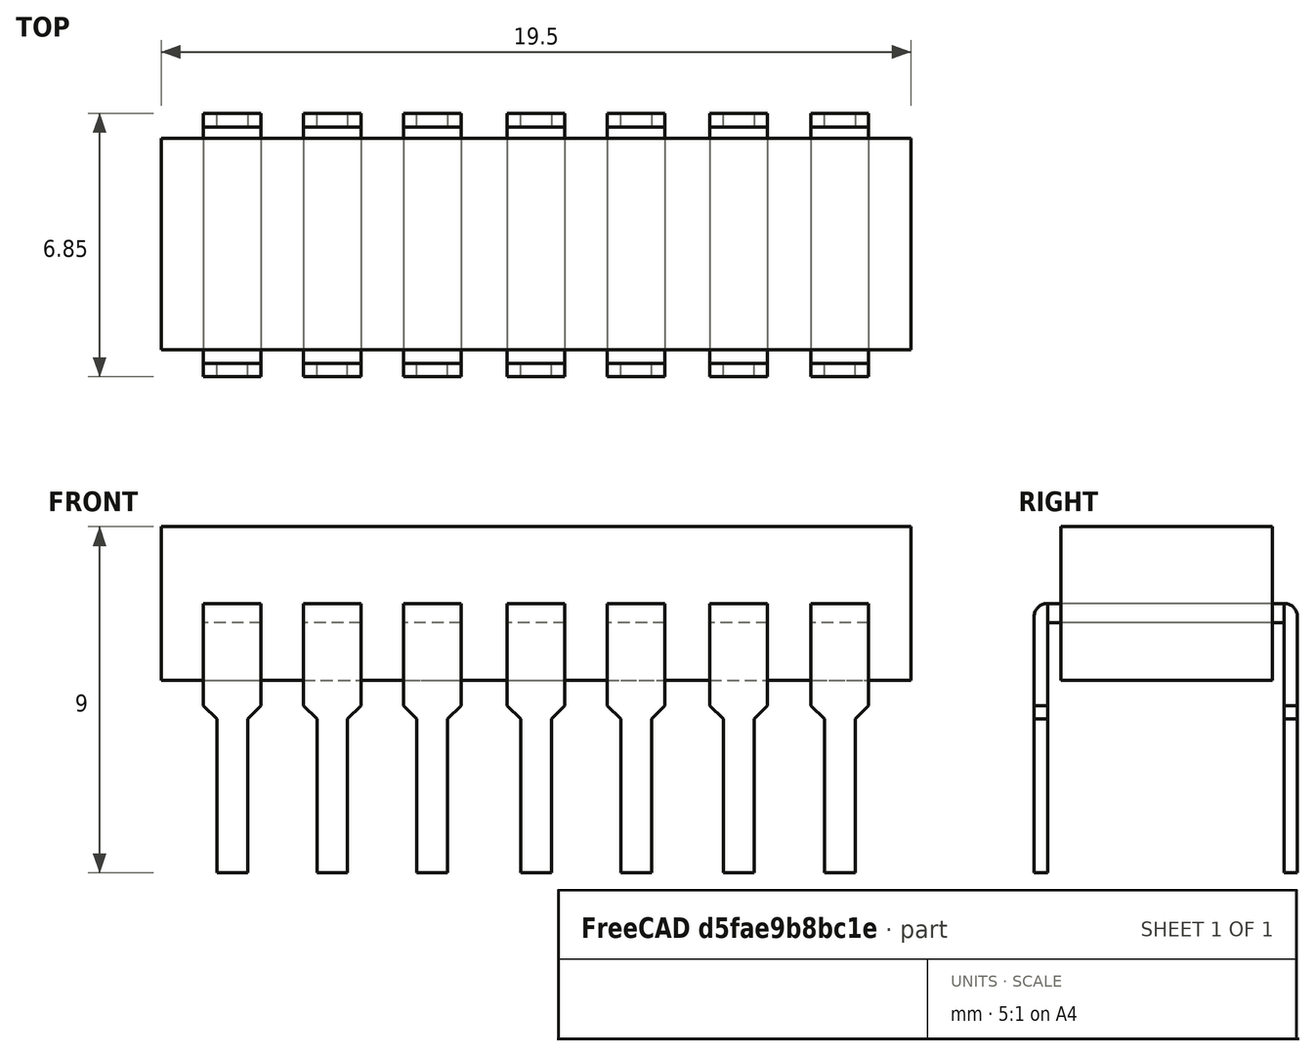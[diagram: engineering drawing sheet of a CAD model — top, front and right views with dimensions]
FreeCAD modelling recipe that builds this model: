
FCSTD DOCUMENT  (FreeCAD 1.0R39319 (Git))
Label: microshem
License: All rights reserved
LicenseURL: https://en.wikipedia.org/wiki/All_rights_reserved
objects: PartDesign::AdditiveBox×36, PartDesign::Chamfer×28, PartDesign::Body×22, PartDesign::Fillet×14, PartDesign::Mirrored×1
note: 258 computed .brp shape members not serialized (recipe doc carries the construction recipe); baked Part::Feature solids carry a one-line shape summary decoded from their .brp

FEATURE [PartDesign::AdditiveBox] Box
  AttacherType = Attacher::AttachEngine3D
  Height = 2
  Length = 19.5
  Placement = pos=(-0.5,0,0) rot=(0,0,1;0rad)
  Refine = true
  Suppressed = false
  Width = 5.5
FEATURE [PartDesign::Mirrored] Mirrored
  BaseFeature = -> Box
  MirrorPlane = -> Box [Face6]
  Originals = -> [Box]
  Placement = pos=(-0.5,0,0) rot=(0,0,1;0rad)
  Refine = true
  Suppressed = false
  TransformMode = 0
FEATURE [PartDesign::Body] Body
  AllowCompound = false
  Group = -> [Box,Mirrored]
  Origin = -> Origin
  Tip = -> Mirrored
FEATURE [PartDesign::AdditiveBox] Box001
  AttacherType = Attacher::AttachEngine3D
  AttachmentOffset = pos=(1.5,-0.7,-1) rot=(0,0,1;0rad)
  AttachmentSupport = -> [X_Axis001]
  Height = 3
  Length = 1.5
  MapMode = 2
  Placement = pos=(1.5,-0.7,-1) rot=(0,0,1;0rad)
  Refine = true
  Suppressed = false
  Width = 0.35
FEATURE [PartDesign::Chamfer] Chamfer
  Angle = 45
  Base = -> Box001 [Edge8]
  BaseFeature = -> Box001
  ChamferType = 0
  FlipDirection = false
  Placement = pos=(1.5,-0.7,-1) rot=(0,0,1;0rad)
  Refine = true
  Size = 0.35
  Size2 = 1
  SupportTransform = false
  Suppressed = false
  UseAllEdges = false
FEATURE [PartDesign::Fillet] Fillet
  Base = -> Chamfer [Edge8]
  BaseFeature = -> Chamfer
  Placement = pos=(1.5,-0.7,-1) rot=(0,0,1;0rad)
  Radius = 0.34
  Refine = true
  SupportTransform = false
  Suppressed = false
  UseAllEdges = false
FEATURE [PartDesign::Chamfer] Chamfer001
  Angle = 45
  Base = -> Fillet [Edge18]
  BaseFeature = -> Fillet
  ChamferType = 0
  FlipDirection = false
  Placement = pos=(1.5,-0.7,-1) rot=(0,0,1;0rad)
  Refine = true
  Size = 0.35
  Size2 = 1
  SupportTransform = false
  Suppressed = false
  UseAllEdges = false
FEATURE [PartDesign::AdditiveBox] Box003
  AttacherType = Attacher::AttachEngine3D
  AttachmentOffset = pos=(-0.35,-4,-0.8) rot=(0,0,1;0rad)
  AttachmentSupport = -> [Chamfer001]
  BaseFeature = -> Chamfer001
  Height = 0.8
  Length = 0.35
  MapMode = 7
  Placement = pos=(2.65,-0.35,-5) rot=(0.57735,-0.57735,-0.57735;2.0944rad)
  Refine = true
  Suppressed = false
  Width = 4
FEATURE [PartDesign::Body] Body001  label="Тіло"
  AllowCompound = false
  Group = -> [Box001,Chamfer,Fillet,Chamfer001,Box003]
  Origin = -> Origin001
  Placement = pos=(14.9,0,0) rot=(0,0,1;0rad)
  Tip = -> Box003
FEATURE [PartDesign::AdditiveBox] Box004
  AttacherType = Attacher::AttachEngine3D
  AttachmentOffset = pos=(-1.13,-0.7,-1) rot=(0,0,1;0rad)
  AttachmentSupport = -> [X_Axis002]
  Height = 3
  Length = 1.5
  MapMode = 2
  Placement = pos=(-1.13,-0.7,-1) rot=(0,0,1;0rad)
  Refine = true
  Suppressed = false
  Width = 0.35
FEATURE [PartDesign::Chamfer] Chamfer002
  Angle = 45
  Base = -> Box004 [Edge8]
  BaseFeature = -> Box004
  ChamferType = 0
  FlipDirection = false
  Placement = pos=(-1.13,-0.7,-1) rot=(0,0,1;0rad)
  Refine = true
  Size = 0.35
  Size2 = 1
  SupportTransform = false
  Suppressed = false
  UseAllEdges = false
FEATURE [PartDesign::Fillet] Fillet001
  Base = -> Chamfer002 [Edge8]
  BaseFeature = -> Chamfer002
  Placement = pos=(-1.13,-0.7,-1) rot=(0,0,1;0rad)
  Radius = 0.34
  Refine = true
  SupportTransform = false
  Suppressed = false
  UseAllEdges = false
FEATURE [PartDesign::Chamfer] Chamfer003
  Angle = 45
  Base = -> Fillet001 [Edge18]
  BaseFeature = -> Fillet001
  ChamferType = 0
  FlipDirection = false
  Placement = pos=(-1.13,-0.7,-1) rot=(0,0,1;0rad)
  Refine = true
  Size = 0.35
  Size2 = 1
  SupportTransform = false
  Suppressed = false
  UseAllEdges = false
FEATURE [PartDesign::AdditiveBox] Box005
  AttacherType = Attacher::AttachEngine3D
  AttachmentOffset = pos=(-0.35,-4,-0.8) rot=(0,0,1;0rad)
  AttachmentSupport = -> [Chamfer003]
  BaseFeature = -> Chamfer003
  Height = 0.8
  Length = 0.35
  MapMode = 7
  Placement = pos=(0.02,-0.35,-5) rot=(0.57735,-0.57735,-0.57735;2.0944rad)
  Refine = true
  Suppressed = false
  Width = 4
FEATURE [PartDesign::Body] Body002  label="Тіло001"
  AllowCompound = false
  Group = -> [Box004,Chamfer002,Fillet001,Chamfer003,Box005]
  Origin = -> Origin002
  Placement = pos=(14.9,0,0) rot=(0,0,1;0rad)
  Tip = -> Box005
FEATURE [PartDesign::AdditiveBox] Box006
  AttacherType = Attacher::AttachEngine3D
  AttachmentOffset = pos=(-3.8,-0.7,-1) rot=(0,0,1;0rad)
  AttachmentSupport = -> [X_Axis003]
  Height = 3
  Length = 1.5
  MapMode = 2
  Placement = pos=(-3.8,-0.7,-1) rot=(0,0,1;0rad)
  Refine = true
  Suppressed = false
  Width = 0.35
FEATURE [PartDesign::Chamfer] Chamfer004
  Angle = 45
  Base = -> Box006 [Edge8]
  BaseFeature = -> Box006
  ChamferType = 0
  FlipDirection = false
  Placement = pos=(-3.8,-0.7,-1) rot=(0,0,1;0rad)
  Refine = true
  Size = 0.35
  Size2 = 1
  SupportTransform = false
  Suppressed = false
  UseAllEdges = false
FEATURE [PartDesign::Fillet] Fillet002
  Base = -> Chamfer004 [Edge8]
  BaseFeature = -> Chamfer004
  Placement = pos=(-3.8,-0.7,-1) rot=(0,0,1;0rad)
  Radius = 0.34
  Refine = true
  SupportTransform = false
  Suppressed = false
  UseAllEdges = false
FEATURE [PartDesign::Chamfer] Chamfer005
  Angle = 45
  Base = -> Fillet002 [Edge18]
  BaseFeature = -> Fillet002
  ChamferType = 0
  FlipDirection = false
  Placement = pos=(-3.8,-0.7,-1) rot=(0,0,1;0rad)
  Refine = true
  Size = 0.35
  Size2 = 1
  SupportTransform = false
  Suppressed = false
  UseAllEdges = false
FEATURE [PartDesign::AdditiveBox] Box007
  AttacherType = Attacher::AttachEngine3D
  AttachmentOffset = pos=(-0.35,-4,-0.8) rot=(0,0,1;0rad)
  AttachmentSupport = -> [Chamfer005]
  BaseFeature = -> Chamfer005
  Height = 0.8
  Length = 0.35
  MapMode = 7
  Placement = pos=(-2.65,-0.35,-5) rot=(0.57735,-0.57735,-0.57735;2.0944rad)
  Refine = true
  Suppressed = false
  Width = 4
FEATURE [PartDesign::Body] Body003  label="Тіло002"
  AllowCompound = false
  Group = -> [Box006,Chamfer004,Fillet002,Chamfer005,Box007]
  Origin = -> Origin003
  Placement = pos=(14.9,0,0) rot=(0,0,1;0rad)
  Tip = -> Box007
FEATURE [PartDesign::AdditiveBox] Box008
  AttacherType = Attacher::AttachEngine3D
  AttachmentOffset = pos=(-6.4,-0.7,-1) rot=(0,0,1;0rad)
  AttachmentSupport = -> [X_Axis004]
  Height = 3
  Length = 1.5
  MapMode = 2
  Placement = pos=(-6.4,-0.7,-1) rot=(0,0,1;0rad)
  Refine = true
  Suppressed = false
  Width = 0.35
FEATURE [PartDesign::Chamfer] Chamfer006
  Angle = 45
  Base = -> Box008 [Edge8]
  BaseFeature = -> Box008
  ChamferType = 0
  FlipDirection = false
  Placement = pos=(-6.4,-0.7,-1) rot=(0,0,1;0rad)
  Refine = true
  Size = 0.35
  Size2 = 1
  SupportTransform = false
  Suppressed = false
  UseAllEdges = false
FEATURE [PartDesign::Fillet] Fillet003
  Base = -> Chamfer006 [Edge8]
  BaseFeature = -> Chamfer006
  Placement = pos=(-6.4,-0.7,-1) rot=(0,0,1;0rad)
  Radius = 0.34
  Refine = true
  SupportTransform = false
  Suppressed = false
  UseAllEdges = false
FEATURE [PartDesign::Chamfer] Chamfer007
  Angle = 45
  Base = -> Fillet003 [Edge18]
  BaseFeature = -> Fillet003
  ChamferType = 0
  FlipDirection = false
  Placement = pos=(-6.4,-0.7,-1) rot=(0,0,1;0rad)
  Refine = true
  Size = 0.35
  Size2 = 1
  SupportTransform = false
  Suppressed = false
  UseAllEdges = false
FEATURE [PartDesign::AdditiveBox] Box009
  AttacherType = Attacher::AttachEngine3D
  AttachmentOffset = pos=(-0.35,-4,-0.8) rot=(0,0,1;0rad)
  AttachmentSupport = -> [Chamfer007]
  BaseFeature = -> Chamfer007
  Height = 0.8
  Length = 0.35
  MapMode = 7
  Placement = pos=(-5.25,-0.35,-5) rot=(0.57735,-0.57735,-0.57735;2.0944rad)
  Refine = true
  Suppressed = false
  Width = 4
FEATURE [PartDesign::Body] Body004  label="Тіло003"
  AllowCompound = false
  Group = -> [Box008,Chamfer006,Fillet003,Chamfer007,Box009]
  Origin = -> Origin004
  Placement = pos=(14.9,0,0) rot=(0,0,1;0rad)
  Tip = -> Box009
FEATURE [PartDesign::AdditiveBox] Box010
  AttacherType = Attacher::AttachEngine3D
  AttachmentOffset = pos=(-9.1,-0.7,-1) rot=(0,0,1;0rad)
  AttachmentSupport = -> [X_Axis005]
  Height = 3
  Length = 1.5
  MapMode = 2
  Placement = pos=(-9.1,-0.7,-1) rot=(0,0,1;0rad)
  Refine = true
  Suppressed = false
  Width = 0.35
FEATURE [PartDesign::Chamfer] Chamfer008
  Angle = 45
  Base = -> Box010 [Edge8]
  BaseFeature = -> Box010
  ChamferType = 0
  FlipDirection = false
  Placement = pos=(-9.1,-0.7,-1) rot=(0,0,1;0rad)
  Refine = true
  Size = 0.35
  Size2 = 1
  SupportTransform = false
  Suppressed = false
  UseAllEdges = false
FEATURE [PartDesign::Fillet] Fillet004
  Base = -> Chamfer008 [Edge8]
  BaseFeature = -> Chamfer008
  Placement = pos=(-9.1,-0.7,-1) rot=(0,0,1;0rad)
  Radius = 0.34
  Refine = true
  SupportTransform = false
  Suppressed = false
  UseAllEdges = false
FEATURE [PartDesign::Chamfer] Chamfer009
  Angle = 45
  Base = -> Fillet004 [Edge18]
  BaseFeature = -> Fillet004
  ChamferType = 0
  FlipDirection = false
  Placement = pos=(-9.1,-0.7,-1) rot=(0,0,1;0rad)
  Refine = true
  Size = 0.35
  Size2 = 1
  SupportTransform = false
  Suppressed = false
  UseAllEdges = false
FEATURE [PartDesign::AdditiveBox] Box011
  AttacherType = Attacher::AttachEngine3D
  AttachmentOffset = pos=(-0.35,-4,-0.8) rot=(0,0,1;0rad)
  AttachmentSupport = -> [Chamfer009]
  BaseFeature = -> Chamfer009
  Height = 0.8
  Length = 0.35
  MapMode = 7
  Placement = pos=(-7.95,-0.35,-5) rot=(0.57735,-0.57735,-0.57735;2.0944rad)
  Refine = true
  Suppressed = false
  Width = 4
FEATURE [PartDesign::Body] Body005  label="Тіло004"
  AllowCompound = false
  Group = -> [Box010,Chamfer008,Fillet004,Chamfer009,Box011]
  Origin = -> Origin005
  Placement = pos=(14.9,0,0) rot=(0,0,1;0rad)
  Tip = -> Box011
FEATURE [PartDesign::AdditiveBox] Box012
  AttacherType = Attacher::AttachEngine3D
  AttachmentOffset = pos=(-11.7,-0.7,-1) rot=(0,0,1;0rad)
  AttachmentSupport = -> [X_Axis006]
  Height = 3
  Length = 1.5
  MapMode = 2
  Placement = pos=(-11.7,-0.7,-1) rot=(0,0,1;0rad)
  Refine = true
  Suppressed = false
  Width = 0.35
FEATURE [PartDesign::Chamfer] Chamfer010
  Angle = 45
  Base = -> Box012 [Edge8]
  BaseFeature = -> Box012
  ChamferType = 0
  FlipDirection = false
  Placement = pos=(-11.7,-0.7,-1) rot=(0,0,1;0rad)
  Refine = true
  Size = 0.35
  Size2 = 1
  SupportTransform = false
  Suppressed = false
  UseAllEdges = false
FEATURE [PartDesign::Fillet] Fillet005
  Base = -> Chamfer010 [Edge8]
  BaseFeature = -> Chamfer010
  Placement = pos=(-11.7,-0.7,-1) rot=(0,0,1;0rad)
  Radius = 0.34
  Refine = true
  SupportTransform = false
  Suppressed = false
  UseAllEdges = false
FEATURE [PartDesign::Chamfer] Chamfer011
  Angle = 45
  Base = -> Fillet005 [Edge18]
  BaseFeature = -> Fillet005
  ChamferType = 0
  FlipDirection = false
  Placement = pos=(-11.7,-0.7,-1) rot=(0,0,1;0rad)
  Refine = true
  Size = 0.35
  Size2 = 1
  SupportTransform = false
  Suppressed = false
  UseAllEdges = false
FEATURE [PartDesign::AdditiveBox] Box013
  AttacherType = Attacher::AttachEngine3D
  AttachmentOffset = pos=(-0.35,-4,-0.8) rot=(0,0,1;0rad)
  AttachmentSupport = -> [Chamfer011]
  BaseFeature = -> Chamfer011
  Height = 0.8
  Length = 0.35
  MapMode = 7
  Placement = pos=(-10.55,-0.35,-5) rot=(0.57735,-0.57735,-0.57735;2.0944rad)
  Refine = true
  Suppressed = false
  Width = 4
FEATURE [PartDesign::Body] Body006  label="Тіло005"
  AllowCompound = false
  Group = -> [Box012,Chamfer010,Fillet005,Chamfer011,Box013]
  Origin = -> Origin006
  Placement = pos=(14.9,0,0) rot=(0,0,1;0rad)
  Tip = -> Box013
FEATURE [PartDesign::AdditiveBox] Box014
  AttacherType = Attacher::AttachEngine3D
  AttachmentOffset = pos=(-14.3,-0.7,-1) rot=(0,0,1;0rad)
  AttachmentSupport = -> [X_Axis007]
  Height = 3
  Length = 1.5
  MapMode = 2
  Placement = pos=(-14.3,-0.7,-1) rot=(0,0,1;0rad)
  Refine = true
  Suppressed = false
  Width = 0.35
FEATURE [PartDesign::Chamfer] Chamfer012
  Angle = 45
  Base = -> Box014 [Edge8]
  BaseFeature = -> Box014
  ChamferType = 0
  FlipDirection = false
  Placement = pos=(-14.3,-0.7,-1) rot=(0,0,1;0rad)
  Refine = true
  Size = 0.35
  Size2 = 1
  SupportTransform = false
  Suppressed = false
  UseAllEdges = false
FEATURE [PartDesign::Fillet] Fillet006
  Base = -> Chamfer012 [Edge8]
  BaseFeature = -> Chamfer012
  Placement = pos=(-14.3,-0.7,-1) rot=(0,0,1;0rad)
  Radius = 0.34
  Refine = true
  SupportTransform = false
  Suppressed = false
  UseAllEdges = false
FEATURE [PartDesign::Chamfer] Chamfer013
  Angle = 45
  Base = -> Fillet006 [Edge18]
  BaseFeature = -> Fillet006
  ChamferType = 0
  FlipDirection = false
  Placement = pos=(-14.3,-0.7,-1) rot=(0,0,1;0rad)
  Refine = true
  Size = 0.35
  Size2 = 1
  SupportTransform = false
  Suppressed = false
  UseAllEdges = false
FEATURE [PartDesign::AdditiveBox] Box015
  AttacherType = Attacher::AttachEngine3D
  AttachmentOffset = pos=(-0.35,-4,-0.8) rot=(0,0,1;0rad)
  AttachmentSupport = -> [Chamfer013]
  BaseFeature = -> Chamfer013
  Height = 0.8
  Length = 0.35
  MapMode = 7
  Placement = pos=(-13.15,-0.35,-5) rot=(0.57735,-0.57735,-0.57735;2.0944rad)
  Refine = true
  Suppressed = false
  Width = 4
FEATURE [PartDesign::Body] Body007  label="Тіло006"
  AllowCompound = false
  Group = -> [Box014,Chamfer012,Fillet006,Chamfer013,Box015]
  Origin = -> Origin007
  Placement = pos=(14.9,0,0) rot=(0,0,1;0rad)
  Tip = -> Box015
FEATURE [PartDesign::AdditiveBox] Box016
  AttacherType = Attacher::AttachEngine3D
  AttachmentOffset = pos=(-14.3,5.8,-1) rot=(0,0,1;0rad)
  AttachmentSupport = -> [X_Axis008]
  Height = 3
  Length = 1.5
  MapMode = 2
  Placement = pos=(-14.3,5.8,-1) rot=(0,0,1;0rad)
  Refine = true
  Suppressed = false
  Width = 0.35
FEATURE [PartDesign::Chamfer] Chamfer014
  Angle = 45
  Base = -> Box016 [Edge8]
  BaseFeature = -> Box016
  ChamferType = 0
  FlipDirection = false
  Placement = pos=(-14.3,5.8,-1) rot=(0,0,1;0rad)
  Refine = true
  Size = 0.35
  Size2 = 1
  SupportTransform = false
  Suppressed = false
  UseAllEdges = false
FEATURE [PartDesign::Chamfer] Chamfer015
  Angle = 45
  Base = -> Chamfer014 [Edge15]
  BaseFeature = -> Chamfer014
  ChamferType = 0
  FlipDirection = false
  Placement = pos=(-14.3,5.8,-1) rot=(0,0,1;0rad)
  Refine = true
  Size = 0.35
  Size2 = 1
  SupportTransform = false
  Suppressed = false
  UseAllEdges = false
FEATURE [PartDesign::AdditiveBox] Box017
  AttacherType = Attacher::AttachEngine3D
  AttachmentOffset = pos=(0,-4,-0.8) rot=(0,0,1;0rad)
  AttachmentSupport = -> [Chamfer015]
  BaseFeature = -> Chamfer015
  Height = 0.8
  Length = 0.35
  MapMode = 7
  Placement = pos=(-13.15,6.15,-5) rot=(0.57735,-0.57735,-0.57735;2.0944rad)
  Refine = true
  Suppressed = false
  Width = 4
FEATURE [PartDesign::Fillet] Fillet007
  Base = -> Box017 [Edge8]
  BaseFeature = -> Box017
  Placement = pos=(-13.15,6.15,-5) rot=(0.57735,-0.57735,-0.57735;2.0944rad)
  Radius = 0.34
  Refine = true
  SupportTransform = false
  Suppressed = false
  UseAllEdges = false
FEATURE [PartDesign::Body] Body008  label="Тіло007"
  AllowCompound = false
  Group = -> [Box016,Chamfer014,Chamfer015,Box017,Fillet007]
  Origin = -> Origin008
  Placement = pos=(14.9,0,0) rot=(0,0,1;0rad)
  Tip = -> Fillet007
FEATURE [PartDesign::AdditiveBox] Box018
  AttacherType = Attacher::AttachEngine3D
  AttachmentOffset = pos=(-11.7,5.8,-1) rot=(0,0,1;0rad)
  AttachmentSupport = -> [X_Axis009]
  Height = 3
  Length = 1.5
  MapMode = 2
  Placement = pos=(-11.7,5.8,-1) rot=(0,0,1;0rad)
  Refine = true
  Suppressed = false
  Width = 0.35
FEATURE [PartDesign::Chamfer] Chamfer016
  Angle = 45
  Base = -> Box018 [Edge8]
  BaseFeature = -> Box018
  ChamferType = 0
  FlipDirection = false
  Placement = pos=(-11.7,5.8,-1) rot=(0,0,1;0rad)
  Refine = true
  Size = 0.35
  Size2 = 1
  SupportTransform = false
  Suppressed = false
  UseAllEdges = false
FEATURE [PartDesign::Chamfer] Chamfer017
  Angle = 45
  Base = -> Chamfer016 [Edge15]
  BaseFeature = -> Chamfer016
  ChamferType = 0
  FlipDirection = false
  Placement = pos=(-11.7,5.8,-1) rot=(0,0,1;0rad)
  Refine = true
  Size = 0.35
  Size2 = 1
  SupportTransform = false
  Suppressed = false
  UseAllEdges = false
FEATURE [PartDesign::AdditiveBox] Box019
  AttacherType = Attacher::AttachEngine3D
  AttachmentOffset = pos=(0,-4,-0.8) rot=(0,0,1;0rad)
  AttachmentSupport = -> [Chamfer017]
  BaseFeature = -> Chamfer017
  Height = 0.8
  Length = 0.35
  MapMode = 7
  Placement = pos=(-10.55,6.15,-5) rot=(0.57735,-0.57735,-0.57735;2.0944rad)
  Refine = true
  Suppressed = false
  Width = 4
FEATURE [PartDesign::Fillet] Fillet008
  Base = -> Box019 [Edge8]
  BaseFeature = -> Box019
  Placement = pos=(-10.55,6.15,-5) rot=(0.57735,-0.57735,-0.57735;2.0944rad)
  Radius = 0.34
  Refine = true
  SupportTransform = false
  Suppressed = false
  UseAllEdges = false
FEATURE [PartDesign::Body] Body009  label="Тіло008"
  AllowCompound = false
  Group = -> [Box018,Chamfer016,Chamfer017,Box019,Fillet008]
  Origin = -> Origin009
  Placement = pos=(14.9,0,0) rot=(0,0,1;0rad)
  Tip = -> Fillet008
FEATURE [PartDesign::AdditiveBox] Box020
  AttacherType = Attacher::AttachEngine3D
  AttachmentOffset = pos=(-9.1,5.8,-1) rot=(0,0,1;0rad)
  AttachmentSupport = -> [X_Axis010]
  Height = 3
  Length = 1.5
  MapMode = 2
  Placement = pos=(-9.1,5.8,-1) rot=(0,0,1;0rad)
  Refine = true
  Suppressed = false
  Width = 0.35
FEATURE [PartDesign::Chamfer] Chamfer018
  Angle = 45
  Base = -> Box020 [Edge8]
  BaseFeature = -> Box020
  ChamferType = 0
  FlipDirection = false
  Placement = pos=(-9.1,5.8,-1) rot=(0,0,1;0rad)
  Refine = true
  Size = 0.35
  Size2 = 1
  SupportTransform = false
  Suppressed = false
  UseAllEdges = false
FEATURE [PartDesign::Chamfer] Chamfer019
  Angle = 45
  Base = -> Chamfer018 [Edge15]
  BaseFeature = -> Chamfer018
  ChamferType = 0
  FlipDirection = false
  Placement = pos=(-9.1,5.8,-1) rot=(0,0,1;0rad)
  Refine = true
  Size = 0.35
  Size2 = 1
  SupportTransform = false
  Suppressed = false
  UseAllEdges = false
FEATURE [PartDesign::AdditiveBox] Box021
  AttacherType = Attacher::AttachEngine3D
  AttachmentOffset = pos=(0,-4,-0.8) rot=(0,0,1;0rad)
  AttachmentSupport = -> [Chamfer019]
  BaseFeature = -> Chamfer019
  Height = 0.8
  Length = 0.35
  MapMode = 7
  Placement = pos=(-7.95,6.15,-5) rot=(0.57735,-0.57735,-0.57735;2.0944rad)
  Refine = true
  Suppressed = false
  Width = 4
FEATURE [PartDesign::Fillet] Fillet009
  Base = -> Box021 [Edge8]
  BaseFeature = -> Box021
  Placement = pos=(-7.95,6.15,-5) rot=(0.57735,-0.57735,-0.57735;2.0944rad)
  Radius = 0.34
  Refine = true
  SupportTransform = false
  Suppressed = false
  UseAllEdges = false
FEATURE [PartDesign::Body] Body010  label="Тіло009"
  AllowCompound = false
  Group = -> [Box020,Chamfer018,Chamfer019,Box021,Fillet009]
  Origin = -> Origin010
  Placement = pos=(14.9,0,0) rot=(0,0,1;0rad)
  Tip = -> Fillet009
FEATURE [PartDesign::AdditiveBox] Box022
  AttacherType = Attacher::AttachEngine3D
  AttachmentOffset = pos=(-6.4,5.8,-1) rot=(0,0,1;0rad)
  AttachmentSupport = -> [X_Axis011]
  Height = 3
  Length = 1.5
  MapMode = 2
  Placement = pos=(-6.4,5.8,-1) rot=(0,0,1;0rad)
  Refine = true
  Suppressed = false
  Width = 0.35
FEATURE [PartDesign::Chamfer] Chamfer020
  Angle = 45
  Base = -> Box022 [Edge8]
  BaseFeature = -> Box022
  ChamferType = 0
  FlipDirection = false
  Placement = pos=(-6.4,5.8,-1) rot=(0,0,1;0rad)
  Refine = true
  Size = 0.35
  Size2 = 1
  SupportTransform = false
  Suppressed = false
  UseAllEdges = false
FEATURE [PartDesign::Chamfer] Chamfer021
  Angle = 45
  Base = -> Chamfer020 [Edge15]
  BaseFeature = -> Chamfer020
  ChamferType = 0
  FlipDirection = false
  Placement = pos=(-6.4,5.8,-1) rot=(0,0,1;0rad)
  Refine = true
  Size = 0.35
  Size2 = 1
  SupportTransform = false
  Suppressed = false
  UseAllEdges = false
FEATURE [PartDesign::AdditiveBox] Box023
  AttacherType = Attacher::AttachEngine3D
  AttachmentOffset = pos=(0,-4,-0.8) rot=(0,0,1;0rad)
  AttachmentSupport = -> [Chamfer021]
  BaseFeature = -> Chamfer021
  Height = 0.8
  Length = 0.35
  MapMode = 7
  Placement = pos=(-5.25,6.15,-5) rot=(0.57735,-0.57735,-0.57735;2.0944rad)
  Refine = true
  Suppressed = false
  Width = 4
FEATURE [PartDesign::Fillet] Fillet010
  Base = -> Box023 [Edge8]
  BaseFeature = -> Box023
  Placement = pos=(-5.25,6.15,-5) rot=(0.57735,-0.57735,-0.57735;2.0944rad)
  Radius = 0.34
  Refine = true
  SupportTransform = false
  Suppressed = false
  UseAllEdges = false
FEATURE [PartDesign::Body] Body011  label="Тіло010"
  AllowCompound = false
  Group = -> [Box022,Chamfer020,Chamfer021,Box023,Fillet010]
  Origin = -> Origin011
  Placement = pos=(14.9,0,0) rot=(0,0,1;0rad)
  Tip = -> Fillet010
FEATURE [PartDesign::AdditiveBox] Box024
  AttacherType = Attacher::AttachEngine3D
  AttachmentOffset = pos=(-3.8,5.8,-1) rot=(0,0,1;0rad)
  AttachmentSupport = -> [X_Axis012]
  Height = 3
  Length = 1.5
  MapMode = 2
  Placement = pos=(-3.8,5.8,-1) rot=(0,0,1;0rad)
  Refine = true
  Suppressed = false
  Width = 0.35
FEATURE [PartDesign::Chamfer] Chamfer022
  Angle = 45
  Base = -> Box024 [Edge8]
  BaseFeature = -> Box024
  ChamferType = 0
  FlipDirection = false
  Placement = pos=(-3.8,5.8,-1) rot=(0,0,1;0rad)
  Refine = true
  Size = 0.35
  Size2 = 1
  SupportTransform = false
  Suppressed = false
  UseAllEdges = false
FEATURE [PartDesign::Chamfer] Chamfer023
  Angle = 45
  Base = -> Chamfer022 [Edge15]
  BaseFeature = -> Chamfer022
  ChamferType = 0
  FlipDirection = false
  Placement = pos=(-3.8,5.8,-1) rot=(0,0,1;0rad)
  Refine = true
  Size = 0.35
  Size2 = 1
  SupportTransform = false
  Suppressed = false
  UseAllEdges = false
FEATURE [PartDesign::AdditiveBox] Box025
  AttacherType = Attacher::AttachEngine3D
  AttachmentOffset = pos=(0,-4,-0.8) rot=(0,0,1;0rad)
  AttachmentSupport = -> [Chamfer023]
  BaseFeature = -> Chamfer023
  Height = 0.8
  Length = 0.35
  MapMode = 7
  Placement = pos=(-2.65,6.15,-5) rot=(0.57735,-0.57735,-0.57735;2.0944rad)
  Refine = true
  Suppressed = false
  Width = 4
FEATURE [PartDesign::Fillet] Fillet011
  Base = -> Box025 [Edge8]
  BaseFeature = -> Box025
  Placement = pos=(-2.65,6.15,-5) rot=(0.57735,-0.57735,-0.57735;2.0944rad)
  Radius = 0.34
  Refine = true
  SupportTransform = false
  Suppressed = false
  UseAllEdges = false
FEATURE [PartDesign::Body] Body012  label="Тіло011"
  AllowCompound = false
  Group = -> [Box024,Chamfer022,Chamfer023,Box025,Fillet011]
  Origin = -> Origin012
  Placement = pos=(14.9,0,0) rot=(0,0,1;0rad)
  Tip = -> Fillet011
FEATURE [PartDesign::AdditiveBox] Box026
  AttacherType = Attacher::AttachEngine3D
  AttachmentOffset = pos=(-1.13,5.8,-1) rot=(0,0,1;0rad)
  AttachmentSupport = -> [X_Axis013]
  Height = 3
  Length = 1.5
  MapMode = 2
  Placement = pos=(-1.13,5.8,-1) rot=(0,0,1;0rad)
  Refine = true
  Suppressed = false
  Width = 0.35
FEATURE [PartDesign::Chamfer] Chamfer024
  Angle = 45
  Base = -> Box026 [Edge8]
  BaseFeature = -> Box026
  ChamferType = 0
  FlipDirection = false
  Placement = pos=(-1.13,5.8,-1) rot=(0,0,1;0rad)
  Refine = true
  Size = 0.35
  Size2 = 1
  SupportTransform = false
  Suppressed = false
  UseAllEdges = false
FEATURE [PartDesign::Chamfer] Chamfer025
  Angle = 45
  Base = -> Chamfer024 [Edge15]
  BaseFeature = -> Chamfer024
  ChamferType = 0
  FlipDirection = false
  Placement = pos=(-1.13,5.8,-1) rot=(0,0,1;0rad)
  Refine = true
  Size = 0.35
  Size2 = 1
  SupportTransform = false
  Suppressed = false
  UseAllEdges = false
FEATURE [PartDesign::AdditiveBox] Box027
  AttacherType = Attacher::AttachEngine3D
  AttachmentOffset = pos=(0,-4,-0.8) rot=(0,0,1;0rad)
  AttachmentSupport = -> [Chamfer025]
  BaseFeature = -> Chamfer025
  Height = 0.8
  Length = 0.35
  MapMode = 7
  Placement = pos=(0.02,6.15,-5) rot=(0.57735,-0.57735,-0.57735;2.0944rad)
  Refine = true
  Suppressed = false
  Width = 4
FEATURE [PartDesign::Fillet] Fillet012
  Base = -> Box027 [Edge8]
  BaseFeature = -> Box027
  Placement = pos=(0.02,6.15,-5) rot=(0.57735,-0.57735,-0.57735;2.0944rad)
  Radius = 0.34
  Refine = true
  SupportTransform = false
  Suppressed = false
  UseAllEdges = false
FEATURE [PartDesign::Body] Body013  label="Тіло012"
  AllowCompound = false
  Group = -> [Box026,Chamfer024,Chamfer025,Box027,Fillet012]
  Origin = -> Origin013
  Placement = pos=(14.9,0,0) rot=(0,0,1;0rad)
  Tip = -> Fillet012
FEATURE [PartDesign::AdditiveBox] Box028
  AttacherType = Attacher::AttachEngine3D
  AttachmentOffset = pos=(1.5,5.8,-1) rot=(0,0,1;0rad)
  AttachmentSupport = -> [X_Axis014]
  Height = 3
  Length = 1.5
  MapMode = 2
  Placement = pos=(1.5,5.8,-1) rot=(0,0,1;0rad)
  Refine = true
  Suppressed = false
  Width = 0.35
FEATURE [PartDesign::Chamfer] Chamfer026
  Angle = 45
  Base = -> Box028 [Edge8]
  BaseFeature = -> Box028
  ChamferType = 0
  FlipDirection = false
  Placement = pos=(1.5,5.8,-1) rot=(0,0,1;0rad)
  Refine = true
  Size = 0.35
  Size2 = 1
  SupportTransform = false
  Suppressed = false
  UseAllEdges = false
FEATURE [PartDesign::Chamfer] Chamfer027
  Angle = 45
  Base = -> Chamfer026 [Edge15]
  BaseFeature = -> Chamfer026
  ChamferType = 0
  FlipDirection = false
  Placement = pos=(1.5,5.8,-1) rot=(0,0,1;0rad)
  Refine = true
  Size = 0.35
  Size2 = 1
  SupportTransform = false
  Suppressed = false
  UseAllEdges = false
FEATURE [PartDesign::AdditiveBox] Box029
  AttacherType = Attacher::AttachEngine3D
  AttachmentOffset = pos=(0,-4,-0.8) rot=(0,0,1;0rad)
  AttachmentSupport = -> [Chamfer027]
  BaseFeature = -> Chamfer027
  Height = 0.8
  Length = 0.35
  MapMode = 7
  Placement = pos=(2.65,6.15,-5) rot=(0.57735,-0.57735,-0.57735;2.0944rad)
  Refine = true
  Suppressed = false
  Width = 4
FEATURE [PartDesign::Fillet] Fillet013
  Base = -> Box029 [Edge8]
  BaseFeature = -> Box029
  Placement = pos=(2.65,6.15,-5) rot=(0.57735,-0.57735,-0.57735;2.0944rad)
  Radius = 0.34
  Refine = true
  SupportTransform = false
  Suppressed = false
  UseAllEdges = false
FEATURE [PartDesign::Body] Body014  label="Тіло013"
  AllowCompound = false
  Group = -> [Box028,Chamfer026,Chamfer027,Box029,Fillet013]
  Origin = -> Origin014
  Placement = pos=(14.9,0,0) rot=(0,0,1;0rad)
  Tip = -> Fillet013
FEATURE [PartDesign::AdditiveBox] Box032
  AttacherType = Attacher::AttachEngine3D
  AttachmentOffset = pos=(0.01,-0.5,-11.2) rot=(0,0,1;0rad)
  AttachmentSupport = -> [Fillet009]
  Height = 1.5
  Length = 6.15
  MapMode = 7
  Placement = pos=(2.1,5.8,1.5) rot=(0.57735,-0.57735,-0.57735;2.0944rad)
  Refine = true
  Suppressed = false
  Width = 0.5
FEATURE [PartDesign::Body] Body015  label="Тіло014"
  AllowCompound = false
  Group = -> [Box032]
  Origin = -> Origin015
  Tip = -> Box032
FEATURE [PartDesign::AdditiveBox] Box033
  AttacherType = Attacher::AttachEngine3D
  AttachmentOffset = pos=(0.01,-0.5,-13.8) rot=(0,0,1;0rad)
  AttachmentSupport = -> [Fillet009]
  Height = 1.5
  Length = 6.15
  MapMode = 7
  Placement = pos=(4.7,5.8,1.5) rot=(0.57735,-0.57735,-0.57735;2.0944rad)
  Refine = true
  Suppressed = false
  Width = 0.5
FEATURE [PartDesign::Body] Body016  label="Тіло015"
  AllowCompound = false
  Group = -> [Box033]
  Origin = -> Origin016
  Tip = -> Box033
FEATURE [PartDesign::AdditiveBox] Box034
  AttacherType = Attacher::AttachEngine3D
  AttachmentOffset = pos=(0.01,-0.5,-16.4) rot=(0,0,1;0rad)
  AttachmentSupport = -> [Fillet009]
  Height = 1.5
  Length = 6.15
  MapMode = 7
  Placement = pos=(7.3,5.8,1.5) rot=(0.57735,-0.57735,-0.57735;2.0944rad)
  Refine = true
  Suppressed = false
  Width = 0.5
FEATURE [PartDesign::Body] Body017  label="Тіло016"
  AllowCompound = false
  Group = -> [Box034]
  Origin = -> Origin017
  Tip = -> Box034
FEATURE [PartDesign::AdditiveBox] Box035
  AttacherType = Attacher::AttachEngine3D
  AttachmentOffset = pos=(0.01,-0.5,-19.1) rot=(0,0,1;0rad)
  AttachmentSupport = -> [Fillet009]
  Height = 1.5
  Length = 6.15
  MapMode = 7
  Placement = pos=(10,5.8,1.5) rot=(0.57735,-0.57735,-0.57735;2.0944rad)
  Refine = true
  Suppressed = false
  Width = 0.5
FEATURE [PartDesign::Body] Body018  label="Тіло017"
  AllowCompound = false
  Group = -> [Box035]
  Origin = -> Origin018
  Tip = -> Box035
FEATURE [PartDesign::AdditiveBox] Box036
  AttacherType = Attacher::AttachEngine3D
  AttachmentOffset = pos=(0.01,-0.5,-21.7) rot=(0,0,1;0rad)
  AttachmentSupport = -> [Fillet009]
  Height = 1.5
  Length = 6.15
  MapMode = 7
  Placement = pos=(12.6,5.8,1.5) rot=(0.57735,-0.57735,-0.57735;2.0944rad)
  Refine = true
  Suppressed = false
  Width = 0.5
FEATURE [PartDesign::Body] Body019  label="Тіло018"
  AllowCompound = false
  Group = -> [Box036]
  Origin = -> Origin019
  Tip = -> Box036
FEATURE [PartDesign::AdditiveBox] Box037
  AttacherType = Attacher::AttachEngine3D
  AttachmentOffset = pos=(0.01,-0.5,-24.37) rot=(0,0,1;0rad)
  AttachmentSupport = -> [Fillet009]
  Height = 1.5
  Length = 6.15
  MapMode = 7
  Placement = pos=(15.27,5.8,1.5) rot=(0.57735,-0.57735,-0.57735;2.0944rad)
  Refine = true
  Suppressed = false
  Width = 0.5
FEATURE [PartDesign::Body] Body020  label="Тіло019"
  AllowCompound = false
  Group = -> [Box037]
  Origin = -> Origin020
  Tip = -> Box037
FEATURE [PartDesign::AdditiveBox] Box038
  AttacherType = Attacher::AttachEngine3D
  AttachmentOffset = pos=(0.01,-0.5,-27) rot=(0,0,1;0rad)
  AttachmentSupport = -> [Fillet009]
  Height = 1.5
  Length = 6.15
  MapMode = 7
  Placement = pos=(17.9,5.8,1.5) rot=(0.57735,-0.57735,-0.57735;2.0944rad)
  Refine = true
  Suppressed = false
  Width = 0.5
FEATURE [PartDesign::Body] Body021  label="Тіло020"
  AllowCompound = false
  Group = -> [Box038]
  Origin = -> Origin021
  Tip = -> Box038
